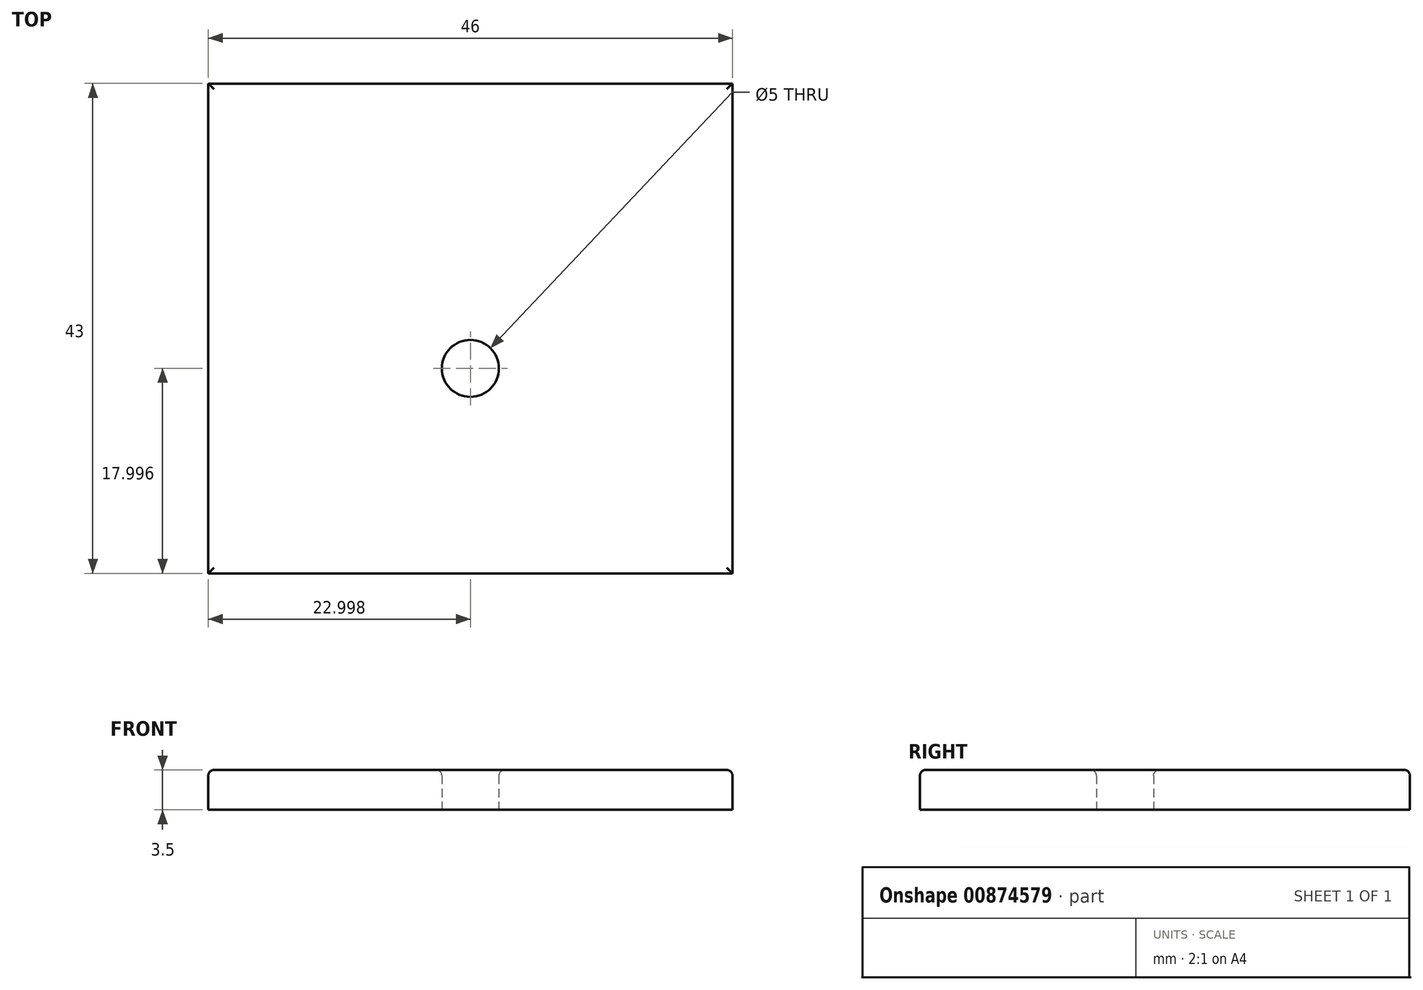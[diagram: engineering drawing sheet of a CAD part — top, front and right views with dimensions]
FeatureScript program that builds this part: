
annotation { "Feature Type Name" : "Feature", "Feature Type Description" : "" }
export const myFeature = defineFeature(function(context is Context, id is Id, definition is map)
    precondition{}
    {
        {
            var Q0;
            Q0=qCreatedBy(makeId("Top.planeOp"),FACE);
            var sketch = newSketch(context, id + "F0", { "sketchPlane" : qUnion([Q0])});
            skLineSegment(sketch, "E0.bottom", {"start": v(19.98, -30.34) * mm, "end": v(-26.02, -30.34) * mm});
            skLineSegment(sketch, "E0.top", {"start": v(19.98, 12.66) * mm, "end": v(-26.02, 12.66) * mm});
            skLineSegment(sketch, "E0.left", {"start": v(19.98, -30.34) * mm, "end": v(19.98, 12.66) * mm});
            skLineSegment(sketch, "E0.right", {"start": v(-26.02, -30.34) * mm, "end": v(-26.02, 12.66) * mm});
            skCircle(sketch, "E1", {"center": v(-3.02, -12.34) * mm, "radius": 2.5 * mm});
            skPoint(sketch, "E1.centerSnap0", {"position": v(-3.02, 12.66) * mm});
            skSolve(sketch);
        }
        {
            var Q0;
            Q0 = qSketchRegion(id + "F0", true);
            extrude(context, id + "F1", {"entities" : qUnion([Q0]), "depth" : 3.5 * mm, "offsetDistance" : 25 * mm});
        }
        {
            var Q0;
            Q0=makeQuery(id+"F1.opExtrude","CAP_FACE",FACE,{"disambiguationData":[OSD([sQuery(id+"F0.wireOp",EDGE,"E0.bottom"),sQuery(id+"F0.wireOp",EDGE,"E0.top"),sQuery(id+"F0.wireOp",EDGE,"E0.left"),sQuery(id+"F0.wireOp",EDGE,"E0.right")])],"isStart":false});
            fillet(context, id + "F2", {"entities" : qUnion([Q0]), "radius" : 0.5 * mm, "tangentPropagation" : true, "allowEdgeOverflow" : false});
        }
    });
